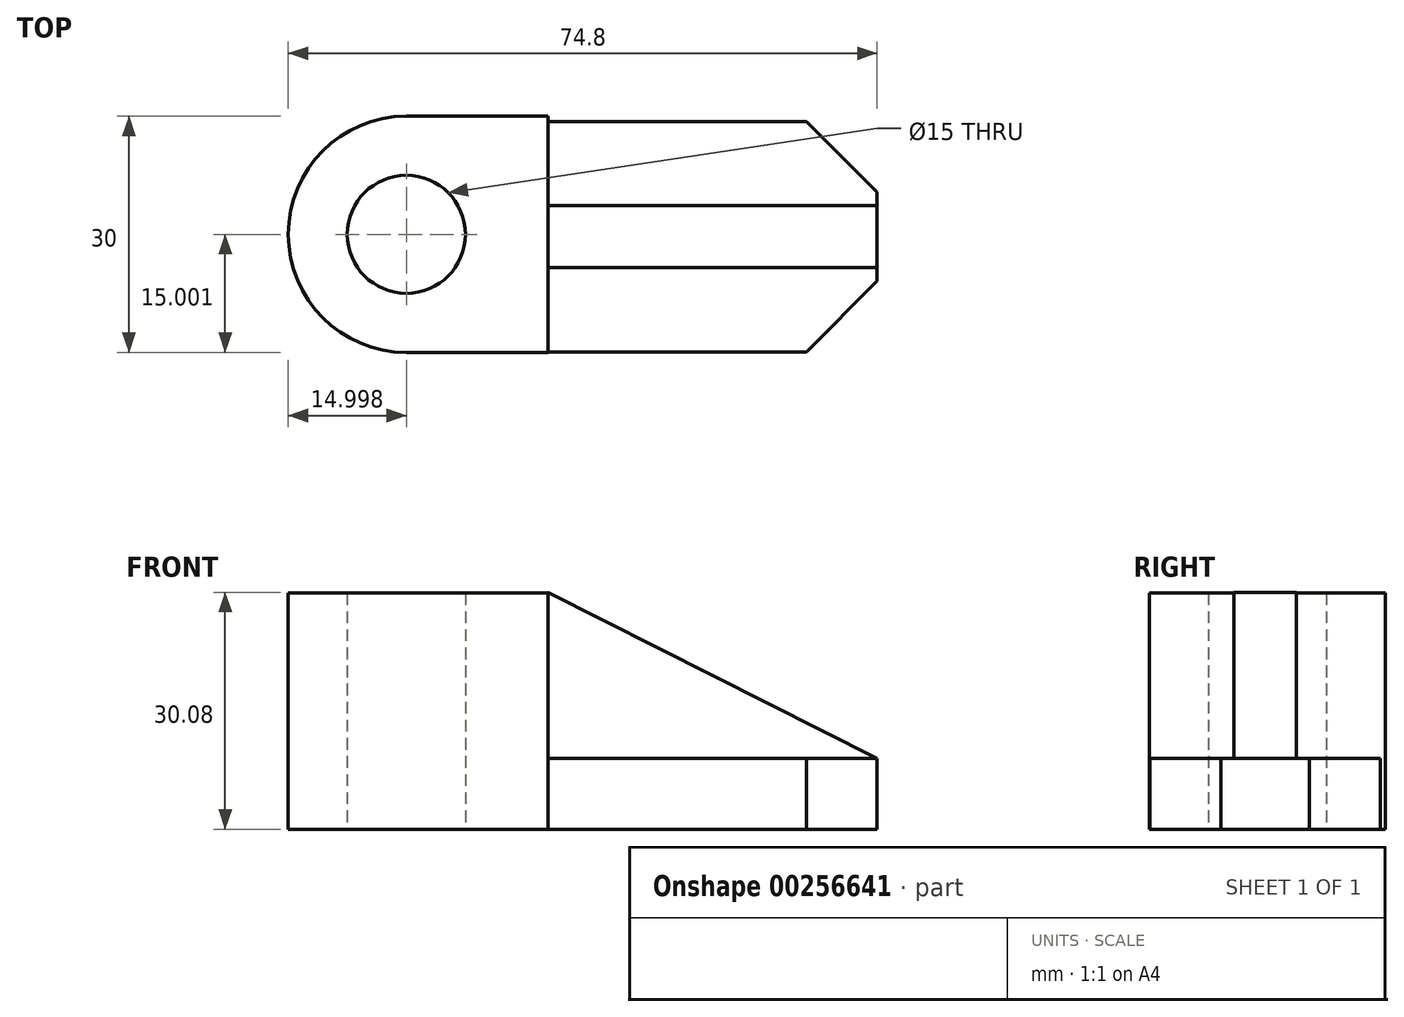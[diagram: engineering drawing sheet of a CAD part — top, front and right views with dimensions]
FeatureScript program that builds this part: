
annotation { "Feature Type Name" : "Feature", "Feature Type Description" : "" }
export const myFeature = defineFeature(function(context is Context, id is Id, definition is map)
    precondition{}
    {
        {
            var Q0;
            Q0=qCreatedBy(makeId("Top.planeOp"),FACE);
            var sketch = newSketch(context, id + "F0", { "sketchPlane" : qUnion([Q0])});
            skLineSegment(sketch, "E0.bottom", {"start": v(-48.05, -16.99) * mm, "end": v(-30.05, -16.99) * mm});
            skLineSegment(sketch, "E0.top", {"start": v(-48.05, 13.01) * mm, "end": v(-30.05, 13.01) * mm});
            skLineSegment(sketch, "E0.left", {"start": v(-48.05, -16.99) * mm, "end": v(-48.05, 13.01) * mm});
            skLineSegment(sketch, "E0.right", {"start": v(-30.05, -16.99) * mm, "end": v(-30.05, 13.01) * mm});
            skArc(sketch, "E1", {"start": v(-48.05, 13.01) * mm, "mid": v(-63.05, -1.99) * mm, "end": v(-48.05, -16.99) * mm});
            skCircle(sketch, "E2", {"center": v(-48.05, -1.99) * mm, "radius": 7.5 * mm});
            skSolve(sketch);
        }
        {
            var Q0;
            {var subQ5=sQuery(id+"F0.wireOp",EDGE,"E0.bottom");Q0=makeQuery(id+"F0.imprint","IMPRINT",FACE,{"disambiguationData":[TD([[makeQuery(id+"F0.imprint","IMPRINT",EDGE,{"derivedFrom":subQ5}),1.0]])]});}
            extrude(context, id + "F1", {"entities" : qUnion([Q0]), "depth" : 30 * mm});
        }
        {
            var Q0;
            {var subQ0=sQuery(id+"F0.wireOp",EDGE,"E1");Q0=makeQuery(id+"F0.imprint","IMPRINT",FACE,{"disambiguationData":[TD([[makeQuery(id+"F0.imprint","IMPRINT",EDGE,{"derivedFrom":subQ0}),1.0]])]});}
            extrude(context, id + "F2", {"entities" : qUnion([Q0]), "operationType" : NewBodyOperationType.ADD, "depth" : 30 * mm});
        }
        {
            var Q0;
            Q0=qCreatedBy(makeId("Top.planeOp"),FACE);
            var sketch = newSketch(context, id + "F3", { "sketchPlane" : qUnion([Q0])});
            skLineSegment(sketch, "E3.bottom", {"start": v(-30.25, -16.92) * mm, "end": v(11.75, -16.92) * mm});
            skLineSegment(sketch, "E3.top", {"start": v(-30.25, 12.35) * mm, "end": v(11.75, 12.35) * mm});
            skLineSegment(sketch, "E3.left", {"start": v(-30.25, -16.92) * mm, "end": v(-30.25, 12.35) * mm});
            skLineSegment(sketch, "E3.right", {"start": v(11.75, -16.92) * mm, "end": v(11.75, 12.35) * mm});
            skSolve(sketch);
        }
        {
            var Q0;
            Q0=makeQuery(id+"F3.imprint","IMPRINT",FACE,{"disambiguationData":[TD([[makeQuery(id+"F3.imprint","IMPRINT",EDGE,{"derivedFrom":sQuery(id+"F3.wireOp",EDGE,"E3.bottom")}),1.0]])]});
            extrude(context, id + "F4", {"entities" : qUnion([Q0]), "operationType" : NewBodyOperationType.ADD, "depth" : 9 * mm});
        }
        {
            var Q0;
            Q0=makeQuery(id+"F4.opExtrude","SWEPT_EDGE",EDGE,{"disambiguationData":[OSD([sQuery(id+"F3.wireOp",EDGE,"E3.bottom"),sQuery(id+"F3.wireOp",EDGE,"E3.right")])]});
            var Q1;
            Q1=makeQuery(id+"F4.opExtrude","SWEPT_EDGE",EDGE,{"disambiguationData":[OSD([sQuery(id+"F3.wireOp",EDGE,"E3.top"),sQuery(id+"F3.wireOp",EDGE,"E3.right")])]});
            chamfer(context, id + "F5", {"entities" : qUnion([Q0, Q1]), "width" : 9 * mm, "tangentPropagation" : true});
        }
        {
            var Q0;
            Q0=makeQuery(id+"F4.opExtrude","CAP_FACE",FACE,{"disambiguationData":[OSD([sQuery(id+"F3.wireOp",EDGE,"E3.bottom"),sQuery(id+"F3.wireOp",EDGE,"E3.top"),sQuery(id+"F3.wireOp",EDGE,"E3.left"),sQuery(id+"F3.wireOp",EDGE,"E3.right")])],"isStart":false});
            var sketch = newSketch(context, id + "F6", { "sketchPlane" : qUnion([Q0])});
            skLineSegment(sketch, "E4", {"start": v(-30.05, -2.28) * mm, "end": v(11.75, -2.28) * mm});
            skLineSegment(sketch, "E5", {"start": v(11.75, -6.24) * mm, "end": v(-30.05, -6.24) * mm});
            skLineSegment(sketch, "E6.MirrorCS", {"start": v(11.75, 1.68) * mm, "end": v(-30.05, 1.68) * mm});
            skSolve(sketch);
        }
        {
            var Q0;
            {var subQ0=sQuery(id+"F6.wireOp",EDGE,"E4");Q0=makeQuery(id+"F6.imprint","IMPRINT",FACE,{"disambiguationData":[TD([[makeQuery(id+"F6.imprint","IMPRINT",EDGE,{"derivedFrom":subQ0}),1.0]])]});}
            var Q1;
            {var subQ0=sQuery(id+"F6.wireOp",EDGE,"E4");Q1=makeQuery(id+"F6.imprint","IMPRINT",FACE,{"disambiguationData":[TD([[makeQuery(id+"F6.imprint","IMPRINT",EDGE,{"derivedFrom":subQ0}),-1.0]])]});}
            extrude(context, id + "F7", {"entities" : qUnion([Q0, Q1]), "operationType" : NewBodyOperationType.ADD, "depth" : 21.08 * mm});
        }
        {
            var Q0;
            Q0=makeQuery(id+"F7.opExtrude","SWEPT_FACE",FACE,{"disambiguationData":[OSD([sQuery(id+"F6.wireOp",EDGE,"E6.MirrorCS")])]});
            var sketch = newSketch(context, id + "F8", { "sketchPlane" : qUnion([Q0])});
            skLineSegment(sketch, "E7", {"start": v(-11.75, 9) * mm, "end": v(30.05, 30.08) * mm});
            skSolve(sketch);
        }
        {
            var Q0;
            Q0=makeQuery(id+"F8.imprint","IMPRINT",FACE,{"disambiguationData":[TD([[makeQuery(id+"F8.imprint","IMPRINT",EDGE,{"derivedFrom":sQuery(id+"F8.wireOp",EDGE,"E7")}),1.0]])]});
            extrude(context, id + "F9", {"entities" : qUnion([Q0]), "operationType" : NewBodyOperationType.REMOVE, "oppositeDirection" : true, "depth" : 25.4 * mm});
        }
    });
